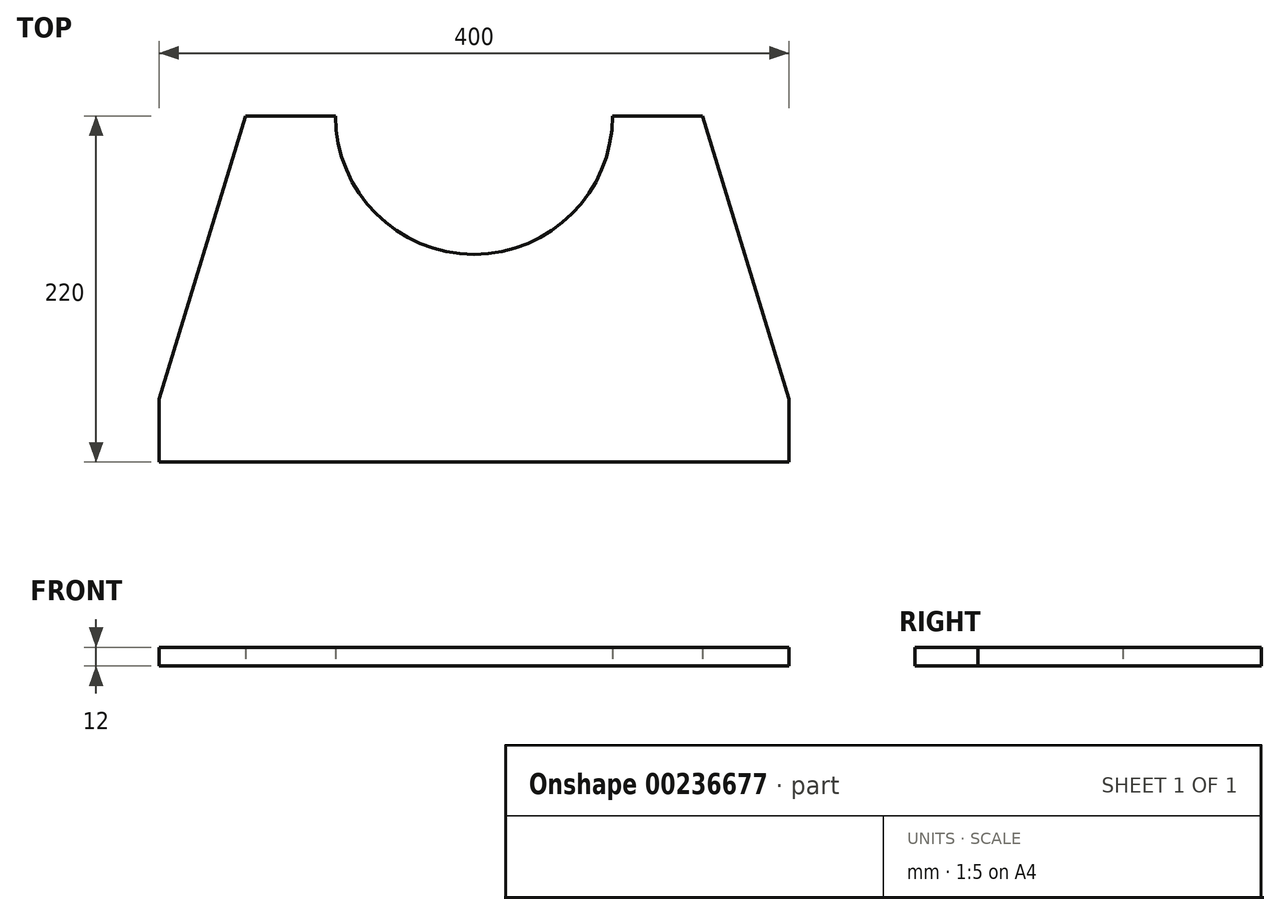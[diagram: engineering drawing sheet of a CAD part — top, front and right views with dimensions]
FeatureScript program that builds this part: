
annotation { "Feature Type Name" : "Feature", "Feature Type Description" : "" }
export const myFeature = defineFeature(function(context is Context, id is Id, definition is map)
    precondition{}
    {
        {
            var Q0;
            Q0=qCreatedBy(makeId("Top.planeOp"),FACE);
            var sketch = newSketch(context, id + "F0", { "sketchPlane" : qUnion([Q0])});
            skLineSegment(sketch, "E0.bottom", {"start": v(0, 0) * mm, "end": v(400, 0) * mm});
            skArc(sketch, "E1", {"start": v(112, 220) * mm, "mid": v(200, 132) * mm, "end": v(288, 220) * mm});
            skLineSegment(sketch, "E2", {"start": v(55, 220) * mm, "end": v(0, 40) * mm});
            skLineSegment(sketch, "E3", {"start": v(345, 220) * mm, "end": v(400, 40) * mm});
            skLineSegment(sketch, "E4", {"start": v(55, 220) * mm, "end": v(112, 220) * mm});
            skLineSegment(sketch, "E5", {"start": v(345, 220) * mm, "end": v(288, 220) * mm});
            skLineSegment(sketch, "E6", {"start": v(0, 40) * mm, "end": v(0, 0) * mm});
            skLineSegment(sketch, "E7", {"start": v(400, 40) * mm, "end": v(400, 0) * mm});
            skSolve(sketch);
        }
        {
            var Q0;
            Q0 = qSketchRegion(id + "F0", true);
            extrude(context, id + "F1", {"entities" : qUnion([Q0]), "depth" : 12 * mm});
        }
    });
